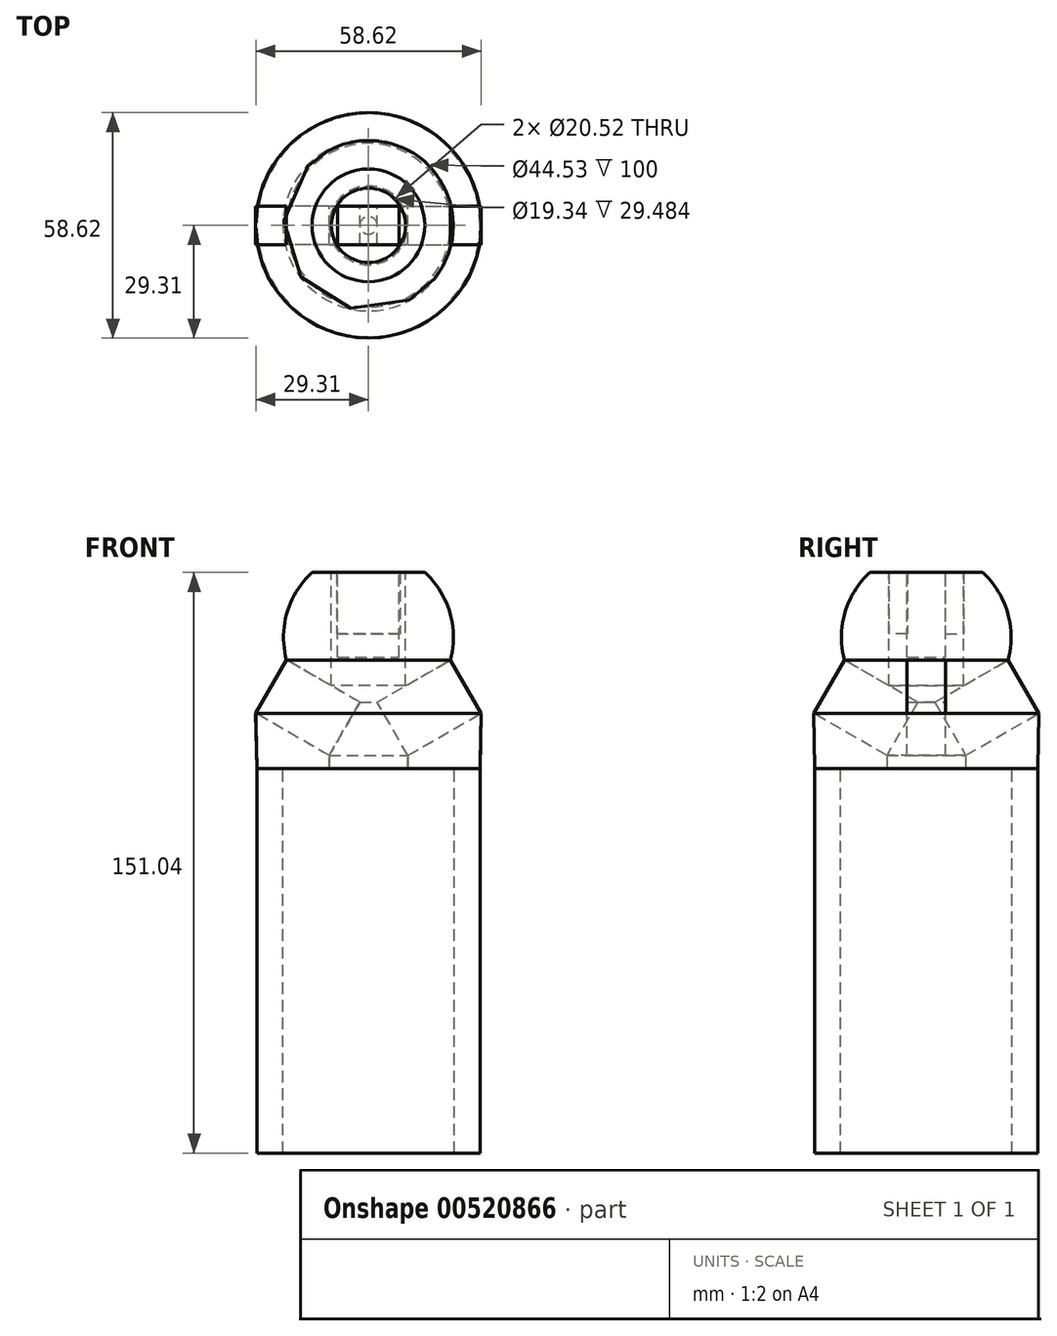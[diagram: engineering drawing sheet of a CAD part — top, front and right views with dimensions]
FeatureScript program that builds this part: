
annotation { "Feature Type Name" : "Feature", "Feature Type Description" : "" }
export const myFeature = defineFeature(function(context is Context, id is Id, definition is map)
    precondition{}
    {
        {
            var Q0;
            Q0=qCreatedBy(makeId("Front.planeOp"),FACE);
            var sketch = newSketch(context, id + "F0", { "sketchPlane" : qUnion([Q0])});
            skLineSegment(sketch, "E0.left", {"start": v(0, 0) * mm, "end": v(0, -100) * mm});
            skLineSegment(sketch, "E1", {"start": v(10.26, 3.43) * mm, "end": v(29.31, 14.43) * mm});
            skLineSegment(sketch, "E2", {"start": v(29.31, 14.43) * mm, "end": v(21.31, 28.28) * mm});
            skLineSegment(sketch, "E3", {"start": v(10.26, 3.43) * mm, "end": v(2.26, 17.28) * mm});
            skLineSegment(sketch, "E4", {"start": v(2.26, 17.28) * mm, "end": v(21.31, 28.28) * mm});
            skLineSegment(sketch, "E5", {"start": v(29.31, 14.43) * mm, "end": v(72, 2.99) * mm});
            skLineSegment(sketch, "E6", {"start": v(0, 29.04) * mm, "end": v(8, 29.04) * mm});
            skLineSegment(sketch, "E7", {"start": v(8, 29.04) * mm, "end": v(8, 51.04) * mm});
            skLineSegment(sketch, "E8", {"start": v(8, 51.04) * mm, "end": v(0, 51.04) * mm});
            skLineSegment(sketch, "E9", {"start": v(8, 51.04) * mm, "end": v(24.95, 67.94) * mm});
            skLineSegment(sketch, "E10", {"start": v(31.18, 65.12) * mm, "end": v(21.31, 28.28) * mm});
            skArc(sketch, "E11", {"start": v(0, 0) * mm, "mid": v(5.4, 0.88) * mm, "end": v(10.26, 3.43) * mm});
            skLineSegment(sketch, "E12.MirrorCS", {"start": v(-8, 51.04) * mm, "end": v(0, 51.04) * mm});
            skLineSegment(sketch, "E13.MirrorCS", {"start": v(-8, 29.04) * mm, "end": v(-8, 51.04) * mm});
            skLineSegment(sketch, "E14.MirrorCS", {"start": v(0, 29.04) * mm, "end": v(-8, 29.04) * mm});
            skArc(sketch, "E15.MirrorCS", {"start": v(-21.31, 28.28) * mm, "mid": v(-19.4, 42.44) * mm, "end": v(-8, 51.04) * mm});
            skLineSegment(sketch, "E16.MirrorCS", {"start": v(-2.26, 17.28) * mm, "end": v(-21.31, 28.28) * mm});
            skLineSegment(sketch, "E17.MirrorCS", {"start": v(-10.26, 3.43) * mm, "end": v(-2.26, 17.28) * mm});
            skLineSegment(sketch, "E18.MirrorCS", {"start": v(-10.26, 3.43) * mm, "end": v(-29.31, 14.43) * mm});
            skLineSegment(sketch, "E19.MirrorCS", {"start": v(-29.31, 14.43) * mm, "end": v(-21.31, 28.28) * mm});
            skLineSegment(sketch, "E20.MirrorCS", {"start": v(-29, 0) * mm, "end": v(-29.31, 14.43) * mm});
            skLineSegment(sketch, "E21.MirrorCS", {"start": v(-29.31, 14.43) * mm, "end": v(-72, 2.99) * mm});
            skLineSegment(sketch, "E22.MirrorCS", {"start": v(-31.18, 65.12) * mm, "end": v(-21.31, 28.28) * mm});
            skArc(sketch, "E23.MirrorCS", {"start": v(0, 0) * mm, "mid": v(-5.4, 0.88) * mm, "end": v(-10.26, 3.43) * mm});
            skLineSegment(sketch, "E24.MirrorCS", {"start": v(0, 0) * mm, "end": v(-29, 0) * mm});
            skLineSegment(sketch, "E25.MirrorCS", {"start": v(-29, 0) * mm, "end": v(-29, -100) * mm});
            skLineSegment(sketch, "E26.MirrorCS", {"start": v(0, -100) * mm, "end": v(-29, -100) * mm});
            skLineSegment(sketch, "E27", {"start": v(-8, 51.04) * mm, "end": v(-15.67, 58.71) * mm});
            skLineSegment(sketch, "E28", {"start": v(-22.27, 0) * mm, "end": v(-22.27, -100) * mm});
            skLineSegment(sketch, "E29", {"start": v(0, 29.04) * mm, "end": v(0, 0) * mm});
            skLineSegment(sketch, "E30", {"start": v(-8, 29.04) * mm, "end": v(-8, 20.6) * mm});
            skLineSegment(sketch, "E31", {"start": v(8, 51.04) * mm, "end": v(14.66, 51.04) * mm});
            skArc(sketch, "E32", {"start": v(21.31, 28.28) * mm, "mid": v(21.17, 40.6) * mm, "end": v(14.66, 51.04) * mm});
            skLineSegment(sketch, "E33", {"start": v(9.67, 51.04) * mm, "end": v(9.67, 21.56) * mm});
            skLineSegment(sketch, "E34", {"start": v(0, 0) * mm, "end": v(0, 51.04) * mm});
            skLineSegment(sketch, "E35", {"start": v(-10.26, 3.43) * mm, "end": v(-10.26, 0) * mm});
            skLineSegment(sketch, "E36", {"start": v(8, 51.04) * mm, "end": v(37.04, 80) * mm});
            skLineSegment(sketch, "E37", {"start": v(21.31, 28.28) * mm, "end": v(34.49, 77.45) * mm});
            skLineSegment(sketch, "E38", {"start": v(-8, 51.04) * mm, "end": v(-35.04, 78.08) * mm});
            skLineSegment(sketch, "E39", {"start": v(-31.18, 65.12) * mm, "end": v(-35.04, 78.08) * mm});
            skSolve(sketch);
        }
        {
            var Q0;
            Q0=makeQuery(id+"F0.imprint","IMPRINT",FACE,{"disambiguationData":[TD([[makeQuery(id+"F0.imprint","IMPRINT",EDGE,{"derivedFrom":sQuery(id+"F0.wireOp",EDGE,"E1")}),1.0]])]});
            var Q1;
            {var subQ0=sQuery(id+"F0.wireOp",EDGE,"E17.MirrorCS");Q1=makeQuery(id+"F0.imprint","IMPRINT",FACE,{"disambiguationData":[TD([[makeQuery(id+"F0.imprint","IMPRINT",EDGE,{"derivedFrom":subQ0}),1.0]])]});}
            var Q2;
            {var subQ0=sQuery(id+"F0.wireOp",EDGE,"E6");Q2=makeQuery(id+"F0.imprint","IMPRINT",FACE,{"disambiguationData":[TD([[makeQuery(id+"F0.imprint","IMPRINT",EDGE,{"derivedFrom":subQ0}),1.0]])]});}
            var Q3;
            {var subQ0=sQuery(id+"F0.wireOp",EDGE,"E12.MirrorCS");Q3=makeQuery(id+"F0.imprint","IMPRINT",FACE,{"disambiguationData":[TD([[makeQuery(id+"F0.imprint","IMPRINT",EDGE,{"derivedFrom":subQ0}),-1.0]])]});}
            extrude(context, id + "F1", {"entities" : qUnion([Q0, Q1, Q2, Q3]), "endBound" : BoundingType.SYMMETRIC, "depth" : 10 * mm, "offsetDistance" : 25 * mm});
        }
        {
            var Q0;
            {var subQ0=sQuery(id+"F0.wireOp",EDGE,"E25.MirrorCS");Q0=makeQuery(id+"F0.imprint","IMPRINT",FACE,{"disambiguationData":[TD([[makeQuery(id+"F0.imprint","IMPRINT",EDGE,{"derivedFrom":subQ0}),1.0]])]});}
            var Q1;
            Q1=sQuery(id+"F0.wireOp",EDGE,"E0.left");
            revolve(context, id + "F2", {"entities" : qUnion([Q0]), "axis" : qUnion([Q1]), "revolveType" : RevolveType.FULL});
        }
        {
            var Q0;
            {var subQ0=sQuery(id+"F0.wireOp",EDGE,"E32");Q0=makeQuery(id+"F0.imprint","IMPRINT",FACE,{"disambiguationData":[TD([[makeQuery(id+"F0.imprint","IMPRINT",EDGE,{"derivedFrom":subQ0}),1.0]])]});}
            var Q1;
            Q1=sQuery(id+"F0.wireOp",EDGE,"E29");
            revolve(context, id + "F3", {"entities" : qUnion([Q0]), "axis" : qUnion([Q1]), "revolveType" : RevolveType.FULL});
        }
        {
            var Q0;
            Q0=qCreatedBy(makeId("Top.planeOp"),FACE);
            var sketch = newSketch(context, id + "F4", { "sketchPlane" : qUnion([Q0])});
            skLineSegment(sketch, "E40", {"start": v(8.22, -4.94) * mm, "end": v(-8.29, -4.94) * mm});
            skArc(sketch, "E41", {"start": v(-8.29, -4.94) * mm, "mid": v(-0.03, -9.74) * mm, "end": v(8.22, -4.94) * mm});
            skLineSegment(sketch, "E42.MirrorCS", {"start": v(8.22, 4.94) * mm, "end": v(-8.29, 4.94) * mm});
            skArc(sketch, "E43.MirrorCS", {"start": v(-8.29, 4.94) * mm, "mid": v(-0.03, 9.74) * mm, "end": v(8.22, 4.94) * mm});
            skSolve(sketch);
        }
        {
            var Q0;
            Q0=makeQuery(id+"F4.imprint","IMPRINT",FACE,{"disambiguationData":[TD([[makeQuery(id+"F4.imprint","IMPRINT",EDGE,{"derivedFrom":sQuery(id+"F4.wireOp",EDGE,"E40")}),1.0]])]});
            extrude(context, id + "F5", {"entities" : qUnion([Q0]), "depth" : 16 * mm, "offsetDistance" : 25 * mm});
        }
        {
            var Q0;
            Q0=makeQuery(id+"F5.opExtrude","SWEPT_BODY",BODY,{"disambiguationData":[OSD([sQuery(id+"F4.wireOp",EDGE,"E40"),sQuery(id+"F4.wireOp",EDGE,"E41")])]});
            var Q1;
            Q1=sQuery(id+"F0.wireOp",VERTEX,"E12.MirrorCS.end");
            transform(context, id + "F6", {"entities" : qUnion([Q0]), "transformType" : TransformType.TRANSLATION_3D, "dx" : 0 * mm, "dy" : 0 * mm, "dz" : 35.04 * mm, "makeCopy" : false});
        }
        {
            var Q0;
            Q0=makeQuery(id+"F4.imprint","IMPRINT",FACE,{"disambiguationData":[TD([[makeQuery(id+"F4.imprint","IMPRINT",EDGE,{"derivedFrom":sQuery(id+"F4.wireOp",EDGE,"E42.MirrorCS")}),-1.0]])]});
            extrude(context, id + "F7", {"entities" : qUnion([Q0]), "depth" : 16 * mm, "offsetDistance" : 25 * mm});
        }
        {
            var Q0;
            Q0=makeQuery(id+"F7.opExtrude","SWEPT_BODY",BODY,{"disambiguationData":[OSD([sQuery(id+"F4.wireOp",EDGE,"E42.MirrorCS"),sQuery(id+"F4.wireOp",EDGE,"E43.MirrorCS")])]});
            transform(context, id + "F8", {"entities" : qUnion([Q0]), "transformType" : TransformType.TRANSLATION_3D, "dx" : 0 * mm, "dy" : 0 * mm, "dz" : 35.04 * mm, "makeCopy" : false});
        }
        {
            var Q0;
            Q0=makeQuery(id+"F0.imprint","IMPRINT",FACE,{"disambiguationData":[TD([[makeQuery(id+"F0.imprint","IMPRINT",EDGE,{"derivedFrom":sQuery(id+"F0.wireOp",EDGE,"E18.MirrorCS")}),1.0]])]});
            var Q1;
            Q1=sQuery(id+"F0.wireOp",EDGE,"E34");
            revolve(context, id + "F9", {"entities" : qUnion([Q0]), "axis" : qUnion([Q1]), "revolveType" : RevolveType.FULL});
        }
        {
            var Q0;
            Q0=makeQuery(id+"F0.imprint","IMPRINT",FACE,{"disambiguationData":[TD([[makeQuery(id+"F0.imprint","IMPRINT",EDGE,{"derivedFrom":sQuery(id+"F0.wireOp",EDGE,"E18.MirrorCS")}),1.0]])]});
            var Q1;
            Q1=sQuery(id+"F0.wireOp",EDGE,"E0.left");
            revolve(context, id + "F10", {"entities" : qUnion([Q0]), "axis" : qUnion([Q1]), "revolveType" : RevolveType.FULL});
        }
        {
            var Q0;
            Q0=makeQuery(id+"F0.imprint","IMPRINT",FACE,{"disambiguationData":[TD([[makeQuery(id+"F0.imprint","IMPRINT",EDGE,{"derivedFrom":sQuery(id+"F0.wireOp",EDGE,"E1")}),1.0]])]});
            var Q1;
            Q1=sQuery(id+"F0.wireOp",EDGE,"E34");
            revolve(context, id + "F11", {"entities" : qUnion([Q0]), "axis" : qUnion([Q1]), "revolveType" : RevolveType.FULL});
        }
    });
